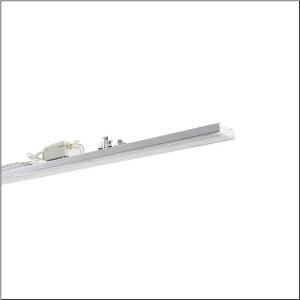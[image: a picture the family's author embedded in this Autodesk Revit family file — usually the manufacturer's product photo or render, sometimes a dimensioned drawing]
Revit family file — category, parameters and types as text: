
# Revit family: licross_11_recessed_mo_51te12cn49xg
name_source: partatom
category: Lighting Fixtures
units: mm (PartAtom-declared; Revit-internal decimal feet)

## family parameters
Cut with Voids When Loaded = No
Host = Face
Light Source = No
Part Type = Normal
Room Calculation Point = No
Round Connector Dimension = Use Diameter
Shared = No

## types (1)
- --- (1 x LED, 9300 lm, 49.3 W, 4000K)
    Apparent Load = 49 VA
    CIE Flux Codes = 67 92 99 100 100
    Color Rendering = 80
    Color Temperature = 4000K
    Default Elevation = 1800 mm
    Description = Licross 11 Recessed MO, luminaire insert, of sheet steel, galvanised, coil coated, white, length: 1.500mm, width: 66mm, height: 67mm, LED rated luminous flux: 9.310lm, light colour: 840, SDCM (Standard Deviation of Colour Matching)MacAdam ≤ 2 SDCM (initial), control gear: ON/OFF Multilumen, CLOi, with plug, 3-pole, with phase selection, mains connection: 220..240V, AC, 50/60Hz, start of lifetime: 49W, end of service life: 55W, internal wiring halogen-free, primary optical cover: cover, of PMMA, light emission: direct distribution, primary light characteristic: symmetric, protection rating (complete): IP54, insulation class (complete): insulation class I (protective earthing), certification: CE, ENEC, VDE, UKCA, protection symbol: D if used in an environment with non-conductive dust loads with corresponding accessories, impact resistance: IK06, permissible ambient temperature for indoor applications: -35..+40°C, corresponds to IFS (International Featured Standards) requirements for safety and quality in the food industry, reducing of maximum allowable ambient temperature of 5°C with ceiling mounting, LABS conformity tested according to VDMA 24364:2018-05, The light source and the operating device comply with the requirements of the Ecodesign Regulation (EU) 2019/2020 and are replaceable in accordance with this regulation, packaging unit: 1 piece
    Height = 58 mm
    Lamp = 1 x LED
    Lamp Light Flux = 9300 lm
    Lamp Power = 49.3 W
    Lamp count = 1
    Length = 1500 mm
    Luminous efficacy = 189 lm/W
    Manufacturer = Siteco
    ModVariant = No
    Model = 51TE12CN49XG
    Mounting Place = Ceiling
    Mounting Type = Pendant
    Number of Poles = 1
    OnlyDefault = Yes
    Power Factor = 1
    Product Name = Licross 11 Recessed MO
    Product group = luminaire insert | ceiling pendant
    ProductGroupID = 901
    Protection Class = Protection class I
    Protection Degree = IP 54
    RLX_Detail_Level = 1
    RLX_Emergency_Light_Flux = 0 lm
    RLX_Emergency_Type = 0
    RLX_Emergency_Type_DB = No
    RlxData = <blob elided: 22513 chars, md5=a757c30e>
    Socket = socket
    Standby Power = 0 W
    System Light Flux = 9300 lm
    System Power = 49 W
    Type Comments = factory setting: luminous flux: 100 % | (A | C | E) | 113 mA
    Type Image = l_1296930.jpg
    URL = http://relux.com
    VarID = @adj_000487
    Voltage = 0 V
    Weight = 0.00 kg
    Width = 66 mm

## geometry (parser evidence)
native form markers: Blend x4, Sweep x10
no freeform markers — native parametric forms only
